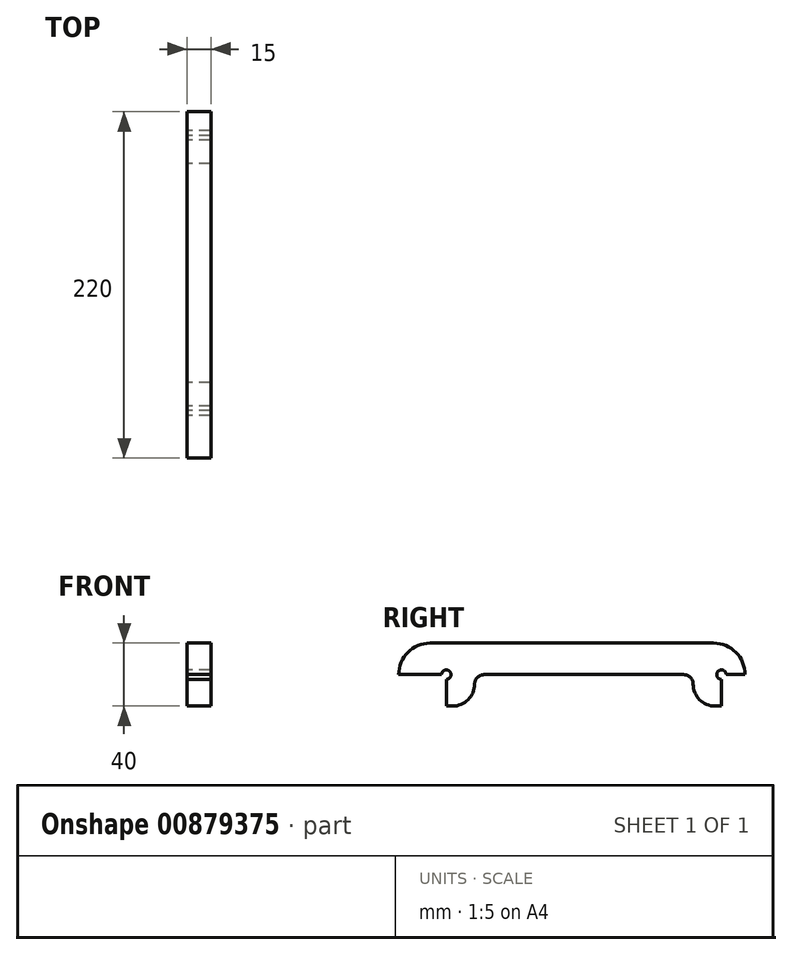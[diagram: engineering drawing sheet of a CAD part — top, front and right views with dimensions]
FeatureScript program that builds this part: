
annotation { "Feature Type Name" : "Feature", "Feature Type Description" : "" }
export const myFeature = defineFeature(function(context is Context, id is Id, definition is map)
    precondition{}
    {
        {
            var Q0;
            Q0=qCreatedBy(makeId("Right.planeOp"),FACE);
            var sketch = newSketch(context, id + "F0", { "sketchPlane" : qUnion([Q0])});
            skLineSegment(sketch, "E0.bottom", {"start": v(-105.36, 44.5) * mm, "end": v(-15.36, 44.5) * mm});
            skLineSegment(sketch, "E0.left", {"start": v(-125.36, 24.5) * mm, "end": v(-125.36, 24.5) * mm});
            skLineSegment(sketch, "E1", {"start": v(-125.36, 24.5) * mm, "end": v(-98.16, 24.5) * mm});
            skLineSegment(sketch, "E2.0", {"start": v(-95.16, 21.5) * mm, "end": v(-95.16, 4.5) * mm});
            skLineSegment(sketch, "E3.0", {"start": v(-77.16, 18.5) * mm, "end": v(-77.16, 18.5) * mm});
            skLineSegment(sketch, "E4.trimOffspring", {"start": v(-71.16, 24.5) * mm, "end": v(-15.36, 24.5) * mm});
            skPoint(sketch, "E5.visualSharp", {"position": v(-125.36, 44.5) * mm});
            skArc(sketch, "E5.filletArc", {"start": v(-105.36, 44.5) * mm, "mid": v(-119.5, 38.64) * mm, "end": v(-125.36, 24.5) * mm});
            skPoint(sketch, "E6.visualSharp", {"position": v(-77.16, 24.5) * mm});
            skArc(sketch, "E6.filletArc", {"start": v(-71.16, 24.5) * mm, "mid": v(-75.4, 22.74) * mm, "end": v(-77.16, 18.5) * mm});
            skArc(sketch, "E7", {"start": v(-95.16, 21.5) * mm, "mid": v(-93.04, 26.62) * mm, "end": v(-98.16, 24.5) * mm});
            skLineSegment(sketch, "E8.bottom", {"start": v(-95.16, 4.5) * mm, "end": v(-91.16, 4.5) * mm});
            skLineSegment(sketch, "E9.MirrorCS", {"start": v(74.64, 44.5) * mm, "end": v(-15.36, 44.5) * mm});
            skArc(sketch, "E10.MirrorCS", {"start": v(74.64, 44.5) * mm, "mid": v(88.78, 38.64) * mm, "end": v(94.64, 24.5) * mm});
            skLineSegment(sketch, "E11.MirrorCS", {"start": v(94.64, 24.5) * mm, "end": v(82.64, 24.5) * mm});
            skArc(sketch, "E12.MirrorC", {"start": v(79.64, 21.5) * mm, "mid": v(77.52, 26.62) * mm, "end": v(82.64, 24.5) * mm});
            skLineSegment(sketch, "E13.MirrorCS", {"start": v(79.64, 21.5) * mm, "end": v(79.64, 4.5) * mm});
            skLineSegment(sketch, "E14.MirrorCS", {"start": v(79.64, 4.5) * mm, "end": v(75.64, 4.5) * mm});
            skArc(sketch, "E15.MirrorCS", {"start": v(55.64, 24.5) * mm, "mid": v(59.88, 22.74) * mm, "end": v(61.64, 18.5) * mm});
            skLineSegment(sketch, "E16.MirrorCS", {"start": v(40.44, 24.5) * mm, "end": v(-15.36, 24.5) * mm});
            skPoint(sketch, "E17.visualSharp", {"position": v(-77.16, 4.5) * mm});
            skArc(sketch, "E17.filletArc", {"start": v(-91.16, 4.5) * mm, "mid": v(-81.26, 8.6) * mm, "end": v(-77.16, 18.5) * mm});
            skArc(sketch, "E18.MirrorCS", {"start": v(75.64, 4.5) * mm, "mid": v(65.74, 8.6) * mm, "end": v(61.64, 18.5) * mm});
            skPoint(sketch, "E19.orphan", {"position": v(61.64, 4.5) * mm});
            skPoint(sketch, "E20.MirrorCS.start.orphan", {"position": v(61.64, 18.5) * mm});
            skLineSegment(sketch, "E21", {"start": v(40.44, 24.5) * mm, "end": v(55.64, 24.5) * mm});
            skSolve(sketch);
        }
        {
            var Q0;
            Q0=makeQuery(id+"F0.imprint","IMPRINT",FACE,{"disambiguationData":[TD([[makeQuery(id+"F0.imprint","IMPRINT",EDGE,{"derivedFrom":sQuery(id+"F0.wireOp",EDGE,"E0.bottom")}),-1.0]])]});
            var Q1;
            Q1=makeQuery(id+"F0.imprint","IMPRINT",FACE,{"disambiguationData":[TD([[makeQuery(id+"F0.imprint","IMPRINT",EDGE,{"derivedFrom":sQuery(id+"F0.wireOp",EDGE,"xPNinXkg-vuuC-jzTt-d5tK-mwDr3JMsSQLC")}),1.0]])]});
            extrude(context, id + "F1", {"entities" : qUnion([Q0, Q1]), "depth" : 15 * mm, "offsetDistance" : 25 * mm});
        }
    });
